# Revit family: Building-ConnessioniIEC309-GEWISS-44IB-PRESE-INTERBLOCCATE_IP44_CON_FONDO_FUS
name_source: partatom
category: Apparecchi elettrici
units: mm (PartAtom-declared; Revit-internal decimal feet)

## family parameters
Condiviso = No
Host = Superficie
Mantenere orientamento annotazione = Sì
Punto di calcolo locali = Sì
Quota connettore circolare = Usa diametro
Taglio con vuoti quando caricato = No
Tipo di parte = Normale

## types (22) — shared parameters
BLOCCO = B=C
Catalogo = BUILDING
Catalogo Serie = 44 IB
Codice Electrocod = 2220
Con fondo = Si
FORMULA = 1000 mm  [stored 3.28084 ft]
Frequenza = 50/60 Hz
Frequenza nominale (Hz) = 50/60 Hz
Glow Wire Test = 850 °C (Parti attive) - 650 °C (Parti passive)
Glow wire test: = 850 °C (Parti attive) - 650 °C (Parti passive)
Grado di protezione = IP44
IDF = 01dac25c-05ac-4859-b7ae-6db1d88bc339
IDT = df42792c-0395-498e-ac0c-0b2d4cd197bd
Immagine tipo = IP44FondoFus.jpg
L = 155 mm  [stored 0.50853 ft]
N.poli = 1
POMELLO = bianco
PRESA = Giallo
Potere di interruzione fusibili = > 50 kA
Produttore = GEWISS S.p.A.
Prospetto di default = 1219 mm
Protezione = Base portafusibile (CBF)
Resistenza agli urti = IK08
SEO = Presa
STRUTTURA = RAL - 7035
STRUTTURA ALTA = blue
Scheda Tecnica = https://www.gewiss.com
Spostamento_S = 1000 mm  [stored 3.28084 ft]
Temperatura di funzionamento = -25 ÷ +40 °C
Temperatura di utilizzo = -25 +40 °C
Termopressione con biglia = 125 °C (Parti attive) - 80 °C (Parti passive)
Tipologia = Orizzontale
URL = https://www.gewiss.com
VETRO = Vetro
Versione file RFA = 21.4
Voltaggio = 0 V
W = 115 mm  [stored 0.377297 ft]

## per-type parameters (varying)
| type | Base portafusibile | Codice EAN | Colore | Colore: | Corrente nominale (A) | Corrente nominale (In) | Descrizione | Modello | N. poli | Numero di poli | Riferimento h | Tensione nominale |
| GW66044 - PRESA BL.OR.C.F.3P+N+T 32A 500V 7H CBF | gG | 8011564006225 | Nero | Nero | 32 | 32 | PRESA BL.OR.C.F.3P+N+T 32A 500V 7H CBF | GW66044 | 3P+N+T | 3P+N+T | 7 | 480-500V |
| GW66025 - PRESA BL.OR.C.F.3P+N+T 16A 110V 4H CBF | E14 | 8011564005976 | Giallo | Giallo | 16 | 16 | PRESA BL.OR.C.F.3P+N+T 16A 110V 4H CBF | GW66025 | 3P+N+T | 3P+N+T | 4 | 100-130V |
| GW66041 - PRESA BL.OR.C.F.3P+T 32A 400V 6H CBF | E18 | 8011564006027 | Rosso | Rosso | 32 | 32 | PRESA BL.OR.C.F.3P+T 32A 400V 6H CBF | GW66041 | 3P+T | 3P+T | 6 | 380-415V |
| GW66034 - PRESA BL.OR.C.F.2P+T 32A 110V 4H CBF | E18 | 8011564006010 | Giallo | Giallo | 32 | 32 | PRESA BL.OR.C.F.2P+T 32A 110V 4H CBF | GW66034 | 2P+T | 2P+T | 4 | 100-130V |
| GW66027 - PRESA BL.OR.C.F.3P+T 16A 230V 9H CBF | E14 | 8011564005914 | Blu | Blu | 16 | 16 | PRESA BL.OR.C.F.3P+T 16A 230V 9H CBF | GW66027 | 3P+T | 3P+T | 9 | 200-250V |
| GW66038 - PRESA BL.OR.C.F.3P+T 32A 230V 9H CBF | E18 | 8011564006065 | Blu | Blu | 32 | 32 | PRESA BL.OR.C.F.3P+T 32A 230V 9H CBF | GW66038 | 3P+T | 3P+T | 9 | 200-250V |
| GW66029 - PRESA BL.OR.C.F.2P+T 16A 400V 9H CBF | E14 | 8011564005945 | Rosso | Rosso | 16 | 16 | PRESA BL.OR.C.F.2P+T 16A 400V 9H CBF | GW66029 | 2P+T | 2P+T | 9 | 380-415V |
| GW66023 - PRESA BL.OR.C.F.2P+T 16A 110V 4H CBF | E14 | 8011564005891 | Giallo | Giallo | 16 | 16 | PRESA BL.OR.C.F.2P+T 16A 110V 4H CBF | GW66023 | 2P+T | 2P+T | 4 | 100-130V |
| GW66042 - PRESA BL.OR.C.F.3P+N+T 32A 400V 6H CBF | E18 | 8011564006034 | Rosso | Rosso | 32 | 32 | PRESA BL.OR.C.F.3P+N+T 32A 400V 6H CBF | GW66042 | 3P+N+T | 3P+N+T | 6 | 380-415V |
| GW66036 - PRESA BL.OR.C.F.3P+N+T 32A 110V 4H CBF | E18 | 8011564006089 | Giallo | Giallo | 32 | 32 | PRESA BL.OR.C.F.3P+N+T 32A 110V 4H CBF | GW66036 | 3P+N+T | 3P+N+T | 4 | 100-130V |
| GW66024 - PRESA BL.OR.C.F.3P+T 16A 110V 4H CBF | E14 | 8011564005952 | Giallo | Giallo | 16 | 16 | PRESA BL.OR.C.F.3P+T 16A 110V 4H CBF | GW66024 | 3P+T | 3P+T | 4 | 100-130V |
| GW66043 - PRESA BL.OR.C.F.3P+T 32A 500V 7H CBF | gG | 8011564006072 | Nero | Nero | 32 | 32 | PRESA BL.OR.C.F.3P+T 32A 500V 7H CBF | GW66043 | 3P+T | 3P+T | 7 | 480-500V |
| GW66035 - PRESA BL.OR.C.F.3P+T 32A 110V 4H CBF | E18 | 8011564006058 | Giallo | Giallo | 32 | 32 | PRESA BL.OR.C.F.3P+T 32A 110V 4H CBF | GW66035 | 3P+T | 3P+T | 4 | 100-130V |
| GW66026 - PRESA BL.OR.C.F.2P+T 16A 230V 6H CBF | E14 | 8011564005907 | Blu | Blu | 16 | 16 | PRESA BL.OR.C.F.2P+T 16A 230V 6H CBF | GW66026 | 2P+T | 2P+T | 6 | 200-250V |
| GW66032 - PRESA BL.OR.C.F.3P+T 16A 500V 7H CBF | gG | 8011564005969 | Nero | Nero | 16 | 16 | PRESA BL.OR.C.F.3P+T 16A 500V 7H CBF | GW66032 | 3P+T | 3P+T | 7 | 480-500V |
| GW66040 - PRESA BL.OR.C.F.2P+T 32A 400V 9H CBF | E18 | 8011564006041 | Rosso | Rosso | 32 | 32 | PRESA BL.OR.C.F.2P+T 32A 400V 9H CBF | GW66040 | 2P+T | 2P+T | 9 | 380-415V |
| GW66028 - PRESA BL.OR.C.F.3P+N+T 16A 230V 9H CBF | E14 | 8011564005983 | Blu | Blu | 16 | 16 | PRESA BL.OR.C.F.3P+N+T 16A 230V 9H CBF | GW66028 | 3P+N+T | 3P+N+T | 9 | 200-250V |
| GW66039 - PRESA BL.OR.C.F.3P+N+T 32A 230V 9H CBF | E18 | 8011564006119 | Blu | Blu | 32 | 32 | PRESA BL.OR.C.F.3P+N+T 32A 230V 9H CBF | GW66039 | 3P+N+T | 3P+N+T | 9 | 200-250V |
| GW66030 - PRESA BL.OR.C.F.3P+T 16A 400V 6H CBF | E14 | 8011564005921 | Rosso | Rosso | 16 | 16 | PRESA BL.OR.C.F.3P+T 16A 400V 6H CBF | GW66030 | 3P+T | 3P+T | 6 | 380-415V |
| GW66033 - PRESA BL.OR.C.F.3P+N+T 16A 500V 7H CBF | gG | 8011564005990 | Nero | Nero | 16 | 16 | PRESA BL.OR.C.F.3P+N+T 16A 500V 7H CBF | GW66033 | 3P+N+T | 3P+N+T | 7 | 480-500V |
| GW66037 - PRESA BL.OR.C.F.2P+T 32A 230V 6H CBF | E18 | 8011564006003 | Blu | Blu | 32 | 32 | PRESA BL.OR.C.F.2P+T 32A 230V 6H CBF | GW66037 | 2P+T | 2P+T | 6 | 200-250V |
| GW66031 - PRESA BL.OR.C.F.3P+N+T 16A 400V 6H CBF | E14 | 8011564005938 | Rosso | Rosso | 16 | 16 | PRESA BL.OR.C.F.3P+N+T 16A 400V 6H CBF | GW66031 | 3P+N+T | 3P+N+T | 6 | 380-415V |

note: [stored X ft] marks values corroborated as IEEE doubles in the binary element streams (Revit-internal decimal feet)

## geometry (parser evidence)
native form markers: Sweep x4
no freeform markers — native parametric forms only
